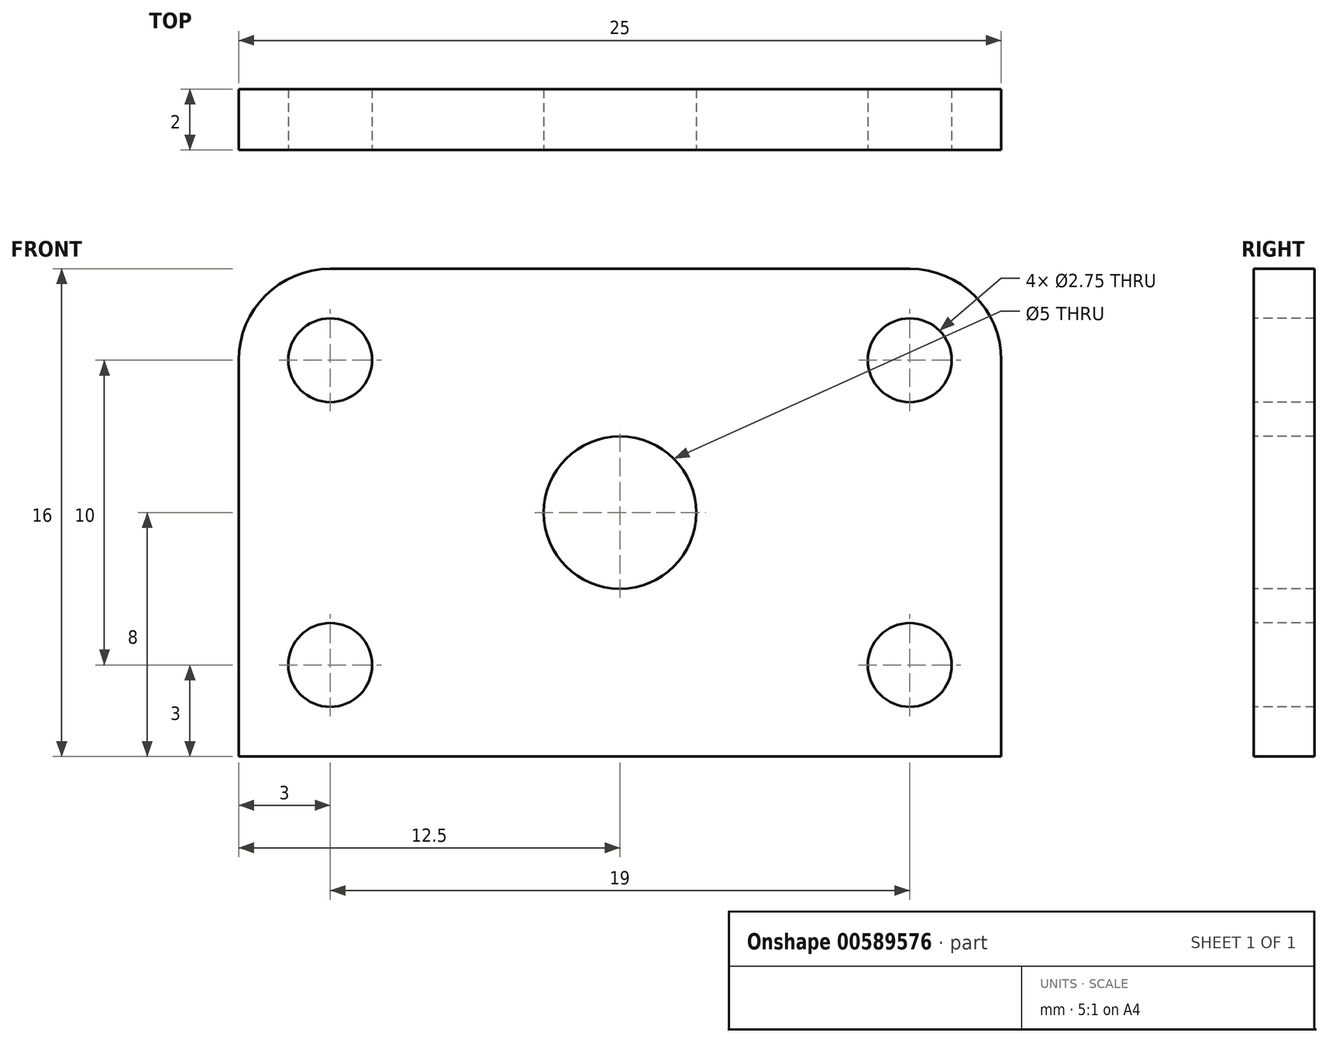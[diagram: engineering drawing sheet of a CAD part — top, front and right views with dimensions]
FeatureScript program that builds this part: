
annotation { "Feature Type Name" : "Feature", "Feature Type Description" : "" }
export const myFeature = defineFeature(function(context is Context, id is Id, definition is map)
    precondition{}
    {
        {
            var Q0;
            Q0=qCreatedBy(makeId("Front.planeOp"),FACE);
            var sketch = newSketch(context, id + "F0", { "sketchPlane" : qUnion([Q0])});
            skLineSegment(sketch, "E0.bottom", {"start": v(0, 0) * mm, "end": v(25, 0) * mm});
            skLineSegment(sketch, "E0.top", {"start": v(0, 16) * mm, "end": v(25, 16) * mm});
            skLineSegment(sketch, "E0.left", {"start": v(0, 0) * mm, "end": v(0, 16) * mm});
            skLineSegment(sketch, "E0.right", {"start": v(25, 0) * mm, "end": v(25, 16) * mm});
            skSolve(sketch);
        }
        {
            var Q0;
            Q0=makeQuery(id+"F0.imprint","IMPRINT",FACE,{"disambiguationData":[TD([[makeQuery(id+"F0.imprint","IMPRINT",EDGE,{"derivedFrom":sQuery(id+"F0.wireOp",EDGE,"E0.bottom")}),1.0]])]});
            extrude(context, id + "F1", {"entities" : qUnion([Q0]), "depth" : 2 * mm, "offsetDistance" : 25 * mm});
        }
        {
            var Q0;
            Q0=makeQuery(id+"F1.opExtrude","CAP_FACE",FACE,{"disambiguationData":[OSD([sQuery(id+"F0.wireOp",EDGE,"E0.bottom"),sQuery(id+"F0.wireOp",EDGE,"E0.top"),sQuery(id+"F0.wireOp",EDGE,"E0.left"),sQuery(id+"F0.wireOp",EDGE,"E0.right")])],"isStart":false});
            var sketch = newSketch(context, id + "F2", { "sketchPlane" : qUnion([Q0])});
            skCircle(sketch, "E1", {"center": v(3, 13) * mm, "radius": 1.38 * mm});
            skSolve(sketch);
        }
        {
            var Q0;
            Q0=makeQuery(id+"F2.imprint","IMPRINT",FACE,{"disambiguationData":[TD([[makeQuery(id+"F2.imprint","IMPRINT",EDGE,{"derivedFrom":sQuery(id+"F2.wireOp",EDGE,"E1")}),-1.0]])]});
            var sketch = newSketch(context, id + "F3", { "sketchPlane" : qUnion([Q0])});
            skCircle(sketch, "E2", {"center": v(3, 3) * mm, "radius": 1.38 * mm});
            skSolve(sketch);
        }
        {
            var Q0;
            Q0=makeQuery(id+"F2.imprint","IMPRINT",FACE,{"disambiguationData":[TD([[makeQuery(id+"F2.imprint","IMPRINT",EDGE,{"derivedFrom":sQuery(id+"F2.wireOp",EDGE,"E1")}),-1.0]])]});
            var sketch = newSketch(context, id + "F4", { "sketchPlane" : qUnion([Q0])});
            skCircle(sketch, "E3", {"center": v(22, 13) * mm, "radius": 1.38 * mm});
            skSolve(sketch);
        }
        {
            var Q0;
            Q0=makeQuery(id+"F2.imprint","IMPRINT",FACE,{"disambiguationData":[TD([[makeQuery(id+"F2.imprint","IMPRINT",EDGE,{"derivedFrom":sQuery(id+"F2.wireOp",EDGE,"E1")}),-1.0]])]});
            var sketch = newSketch(context, id + "F5", { "sketchPlane" : qUnion([Q0])});
            skCircle(sketch, "E4", {"center": v(22, 3) * mm, "radius": 1.38 * mm});
            skSolve(sketch);
        }
        {
            var Q0;
            Q0=makeQuery(id+"F2.imprint","IMPRINT",FACE,{"disambiguationData":[TD([[makeQuery(id+"F2.imprint","IMPRINT",EDGE,{"derivedFrom":sQuery(id+"F2.wireOp",EDGE,"E1")}),1.0]])]});
            extrude(context, id + "F6", {"entities" : qUnion([Q0]), "operationType" : NewBodyOperationType.REMOVE, "oppositeDirection" : true, "depth" : 3 * mm, "offsetDistance" : 25 * mm});
        }
        {
            var Q0;
            Q0=makeQuery(id+"F3.imprint","IMPRINT",FACE,{"disambiguationData":[TD([[makeQuery(id+"F3.imprint","IMPRINT",EDGE,{"derivedFrom":sQuery(id+"F3.wireOp",EDGE,"E2")}),1.0]])]});
            extrude(context, id + "F7", {"entities" : qUnion([Q0]), "operationType" : NewBodyOperationType.REMOVE, "oppositeDirection" : true, "depth" : 3 * mm, "offsetDistance" : 25 * mm});
        }
        {
            var Q0;
            Q0=makeQuery(id+"F4.imprint","IMPRINT",FACE,{"disambiguationData":[TD([[makeQuery(id+"F4.imprint","IMPRINT",EDGE,{"derivedFrom":sQuery(id+"F4.wireOp",EDGE,"E3")}),1.0]])]});
            var Q1;
            Q1=sQuery(id+"F4.wireOp",EDGE,"E3");
            extrude(context, id + "F8", {"entities" : qUnion([Q0]), "operationType" : NewBodyOperationType.REMOVE, "surfaceEntities" : qUnion([Q1]), "oppositeDirection" : true, "depth" : 3 * mm, "offsetDistance" : 25 * mm});
        }
        {
            var Q0;
            Q0=makeQuery(id+"F5.imprint","IMPRINT",FACE,{"disambiguationData":[TD([[makeQuery(id+"F5.imprint","IMPRINT",EDGE,{"derivedFrom":sQuery(id+"F5.wireOp",EDGE,"E4")}),1.0]])]});
            extrude(context, id + "F9", {"entities" : qUnion([Q0]), "operationType" : NewBodyOperationType.REMOVE, "oppositeDirection" : true, "depth" : 3 * mm, "offsetDistance" : 25 * mm});
        }
        {
            var Q0;
            Q0=makeQuery(id+"F1.opExtrude","SWEPT_EDGE",EDGE,{"disambiguationData":[OSD([sQuery(id+"F0.wireOp",EDGE,"E0.top"),sQuery(id+"F0.wireOp",EDGE,"E0.right")])]});
            fillet(context, id + "F10", {"entities" : qUnion([Q0]), "radius" : 3 * mm, "tangentPropagation" : true, "allowEdgeOverflow" : false});
        }
        {
            var Q0;
            Q0=makeQuery(id+"F1.opExtrude","SWEPT_EDGE",EDGE,{"disambiguationData":[OSD([sQuery(id+"F0.wireOp",EDGE,"E0.top"),sQuery(id+"F0.wireOp",EDGE,"E0.left")])]});
            fillet(context, id + "F11", {"entities" : qUnion([Q0]), "radius" : 3 * mm, "tangentPropagation" : true, "allowEdgeOverflow" : false});
        }
        {
            var Q0;
            Q0=makeQuery(id+"F1.opExtrude","CAP_FACE",FACE,{"disambiguationData":[OSD([sQuery(id+"F0.wireOp",EDGE,"E0.bottom"),sQuery(id+"F0.wireOp",EDGE,"E0.top"),sQuery(id+"F0.wireOp",EDGE,"E0.left"),sQuery(id+"F0.wireOp",EDGE,"E0.right")])],"isStart":false});
            var sketch = newSketch(context, id + "F12", { "sketchPlane" : qUnion([Q0])});
            skCircle(sketch, "E5", {"center": v(12.5, 8) * mm, "radius": 2.5 * mm});
            skSolve(sketch);
        }
        {
            var Q0;
            Q0=makeQuery(id+"F12.imprint","IMPRINT",FACE,{"disambiguationData":[TD([[makeQuery(id+"F12.imprint","IMPRINT",EDGE,{"derivedFrom":sQuery(id+"F12.wireOp",EDGE,"E5")}),1.0]])]});
            extrude(context, id + "F13", {"entities" : qUnion([Q0]), "operationType" : NewBodyOperationType.REMOVE, "oppositeDirection" : true, "depth" : 3 * mm, "offsetDistance" : 25 * mm});
        }
    });
